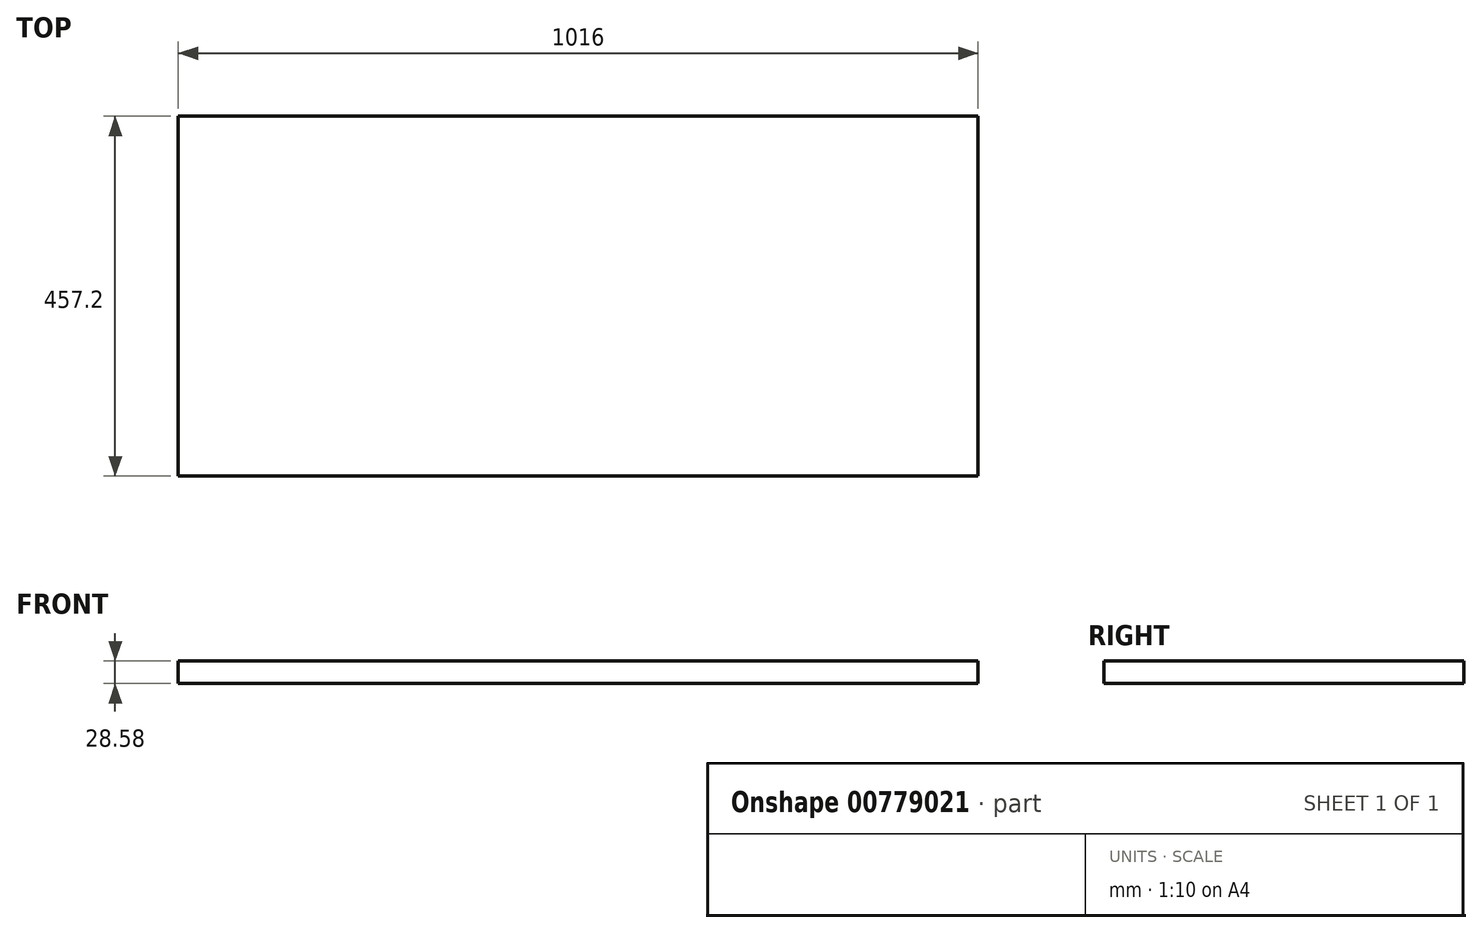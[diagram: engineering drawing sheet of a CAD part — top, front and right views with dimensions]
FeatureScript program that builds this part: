
annotation { "Feature Type Name" : "Feature", "Feature Type Description" : "" }
export const myFeature = defineFeature(function(context is Context, id is Id, definition is map)
    precondition{}
    {
        {
            var Q0;
            Q0=qCreatedBy(makeId("Front.planeOp"),FACE);
            var sketch = newSketch(context, id + "F0", { "sketchPlane" : qUnion([Q0])});
            skLineSegment(sketch, "E0.bottom", {"start": v(-508, -14.29) * mm, "end": v(508, -14.29) * mm});
            skLineSegment(sketch, "E0.top", {"start": v(-508, 14.29) * mm, "end": v(508, 14.29) * mm});
            skLineSegment(sketch, "E0.left", {"start": v(-508, -14.29) * mm, "end": v(-508, 14.29) * mm});
            skLineSegment(sketch, "E0.right", {"start": v(508, -14.29) * mm, "end": v(508, 14.29) * mm});
            skPoint(sketch, "E0.middle", {"position": v(0, 0) * mm});
            skSolve(sketch);
        }
        {
            var Q0;
            Q0=makeQuery(id+"F0.imprint","IMPRINT",FACE,{"disambiguationData":[TD([[makeQuery(id+"F0.imprint","IMPRINT",EDGE,{"derivedFrom":sQuery(id+"F0.wireOp",EDGE,"E0.bottom")}),1.0]])]});
            extrude(context, id + "F1", {"entities" : qUnion([Q0]), "depth" : 457.2 * mm, "offsetDistance" : 25.4 * mm});
        }
    });
